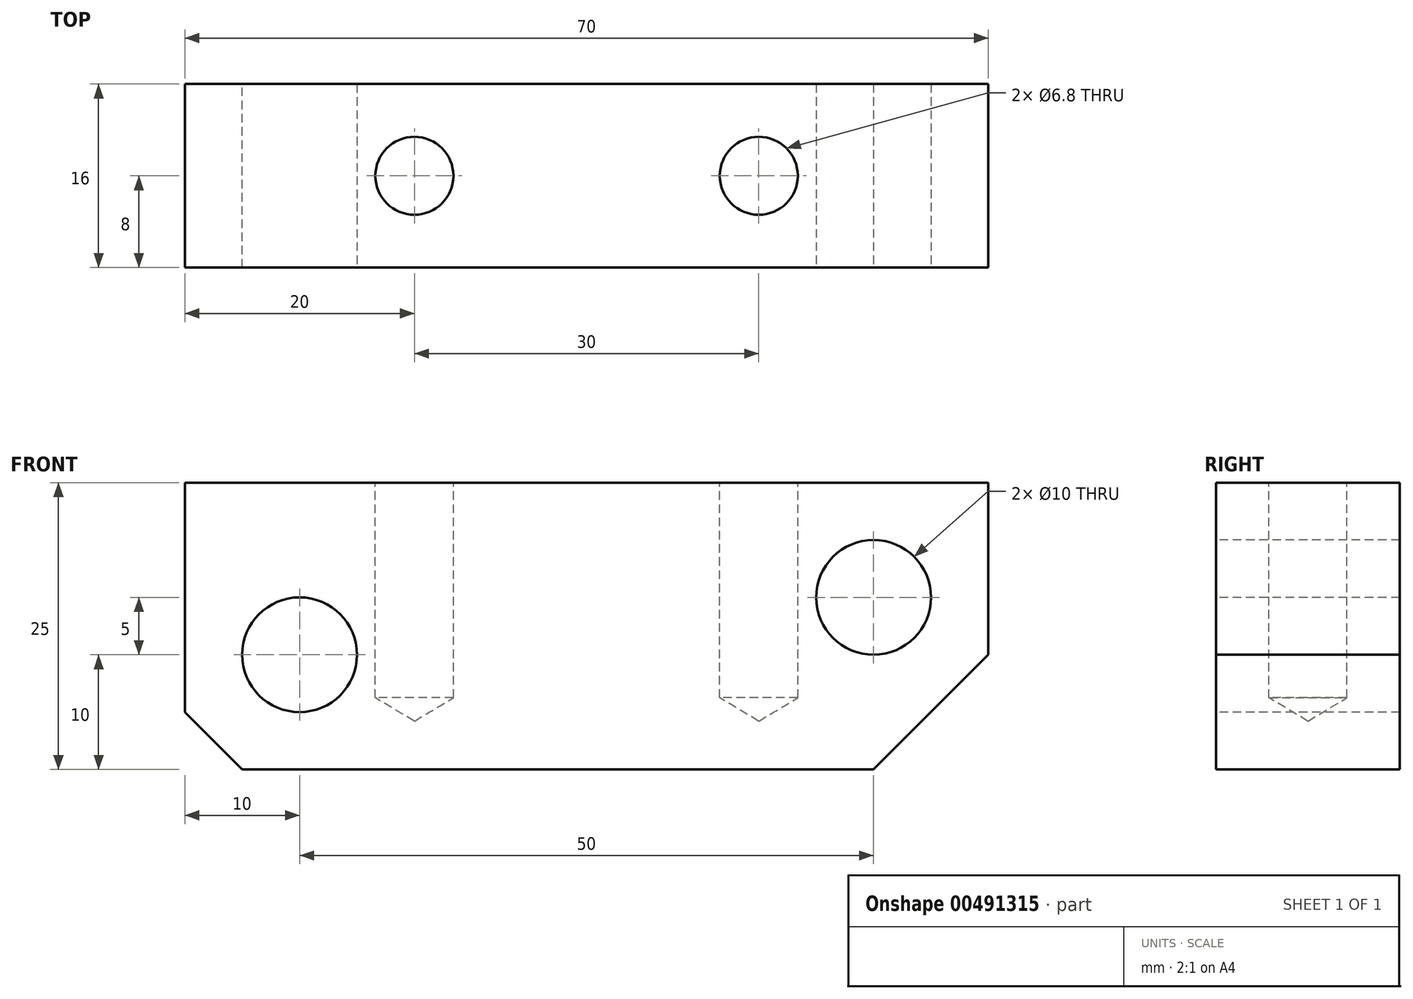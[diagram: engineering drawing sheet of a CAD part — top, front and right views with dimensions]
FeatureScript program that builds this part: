
annotation { "Feature Type Name" : "Feature", "Feature Type Description" : "" }
export const myFeature = defineFeature(function(context is Context, id is Id, definition is map)
    precondition{}
    {
        {
            var Q0;
            Q0=qCreatedBy(makeId("Front.planeOp"),FACE);
            var sketch = newSketch(context, id + "F0", { "sketchPlane" : qUnion([Q0])});
            skLineSegment(sketch, "E0.bottom", {"start": v(-35, 12.5) * mm, "end": v(35, 12.5) * mm});
            skLineSegment(sketch, "E0.top", {"start": v(-35, -12.5) * mm, "end": v(35, -12.5) * mm});
            skLineSegment(sketch, "E0.left", {"start": v(-35, 12.5) * mm, "end": v(-35, -12.5) * mm});
            skLineSegment(sketch, "E0.right", {"start": v(35, 12.5) * mm, "end": v(35, -12.5) * mm});
            skSolve(sketch);
        }
        {
            var Q0;
            Q0=makeQuery(id+"F0.imprint","IMPRINT",FACE,{"disambiguationData":[TD([[makeQuery(id+"F0.imprint","IMPRINT",EDGE,{"derivedFrom":sQuery(id+"F0.wireOp",EDGE,"E0.bottom")}),-1.0]])]});
            extrude(context, id + "F1", {"entities" : qUnion([Q0]), "endBound" : BoundingType.SYMMETRIC, "depth" : 16 * mm});
        }
        {
            var Q0;
            Q0=makeQuery(id+"F1.opExtrude","SWEPT_EDGE",EDGE,{"disambiguationData":[OSD([sQuery(id+"F0.wireOp",EDGE,"E0.top"),sQuery(id+"F0.wireOp",EDGE,"E0.left")])]});
            chamfer(context, id + "F2", {"entities" : qUnion([Q0]), "width" : 5 * mm, "tangentPropagation" : true});
        }
        {
            var Q0;
            Q0=makeQuery(id+"F1.opExtrude","SWEPT_EDGE",EDGE,{"disambiguationData":[OSD([sQuery(id+"F0.wireOp",EDGE,"E0.top"),sQuery(id+"F0.wireOp",EDGE,"E0.right")])]});
            chamfer(context, id + "F3", {"entities" : qUnion([Q0]), "width" : 10 * mm, "tangentPropagation" : true});
        }
        {
            var Q0;
            Q0=makeQuery(id+"F1.opExtrude","CAP_FACE",FACE,{"disambiguationData":[OSD([sQuery(id+"F0.wireOp",EDGE,"E0.bottom"),sQuery(id+"F0.wireOp",EDGE,"E0.top"),sQuery(id+"F0.wireOp",EDGE,"E0.left"),sQuery(id+"F0.wireOp",EDGE,"E0.right")])],"isStart":false});
            var sketch = newSketch(context, id + "F4", { "sketchPlane" : qUnion([Q0])});
            skCircle(sketch, "E1", {"center": v(-25, -2.5) * mm, "radius": 5 * mm});
            skCircle(sketch, "E2", {"center": v(25, 2.5) * mm, "radius": 5 * mm});
            skSolve(sketch);
        }
        {
            var Q0;
            Q0=makeQuery(id+"F4.imprint","IMPRINT",FACE,{"disambiguationData":[TD([[makeQuery(id+"F4.imprint","IMPRINT",EDGE,{"derivedFrom":sQuery(id+"F4.wireOp",EDGE,"E1")}),1.0]])]});
            var Q1;
            Q1=makeQuery(id+"F4.imprint","IMPRINT",FACE,{"disambiguationData":[TD([[makeQuery(id+"F4.imprint","IMPRINT",EDGE,{"derivedFrom":sQuery(id+"F4.wireOp",EDGE,"E2")}),1.0]])]});
            extrude(context, id + "F5", {"entities" : qUnion([Q0, Q1]), "operationType" : NewBodyOperationType.REMOVE, "oppositeDirection" : true, "depth" : 16 * mm});
        }
        {
            var Q0;
            Q0=makeQuery(id+"F1.opExtrude","SWEPT_FACE",FACE,{"disambiguationData":[OSD([sQuery(id+"F0.wireOp",EDGE,"E0.bottom")])]});
            var sketch = newSketch(context, id + "F6", { "sketchPlane" : qUnion([Q0])});
            skPoint(sketch, "E3", {"position": v(-15, 0) * mm});
            skPoint(sketch, "E4", {"position": v(15, 0) * mm});
            skSolve(sketch);
        }
        {
            var Q0;
            Q0=sQuery(id+"F6.wireOp",VERTEX,"E3");
            var Q1;
            Q1=sQuery(id+"F6.wireOp",VERTEX,"E4");
            var Q2;
            Q2=makeQuery(id+"F1.opExtrude","SWEPT_BODY",BODY,{"disambiguationData":[OSD([sQuery(id+"F0.wireOp",EDGE,"E0.bottom"),sQuery(id+"F0.wireOp",EDGE,"E0.top"),sQuery(id+"F0.wireOp",EDGE,"E0.left"),sQuery(id+"F0.wireOp",EDGE,"E0.right")])]});
            hole(context, id + "F7", {"style" : HoleStyle.SIMPLE, "endStyle" : HoleEndStyle.BLIND, "standardTappedOrClearance" : lookupTablePath({ "standard" : "ISO", "engagement" : "75%", "pitch" : "1.25 mm", "size" : "M8", "type" : "Tapped" }), "standardBlindInLast" : lookupTablePath({ "standard" : "ISO", "engagement" : "75%", "pitch" : "1.25 mm", "size" : "M8", "type" : "Tapped" }), "holeDiameter" : 6.8 * mm, "showTappedDepth" : true, "holeDepth" : 18.75 * mm, "isTappedThrough" : true, "tappedDepth" : 15 * mm, "tapClearance" : 3, "locations" : qUnion([Q0, Q1]), "scope" : qUnion([Q2]), "majorDiameter" : 8 * mm});
        }
    });
